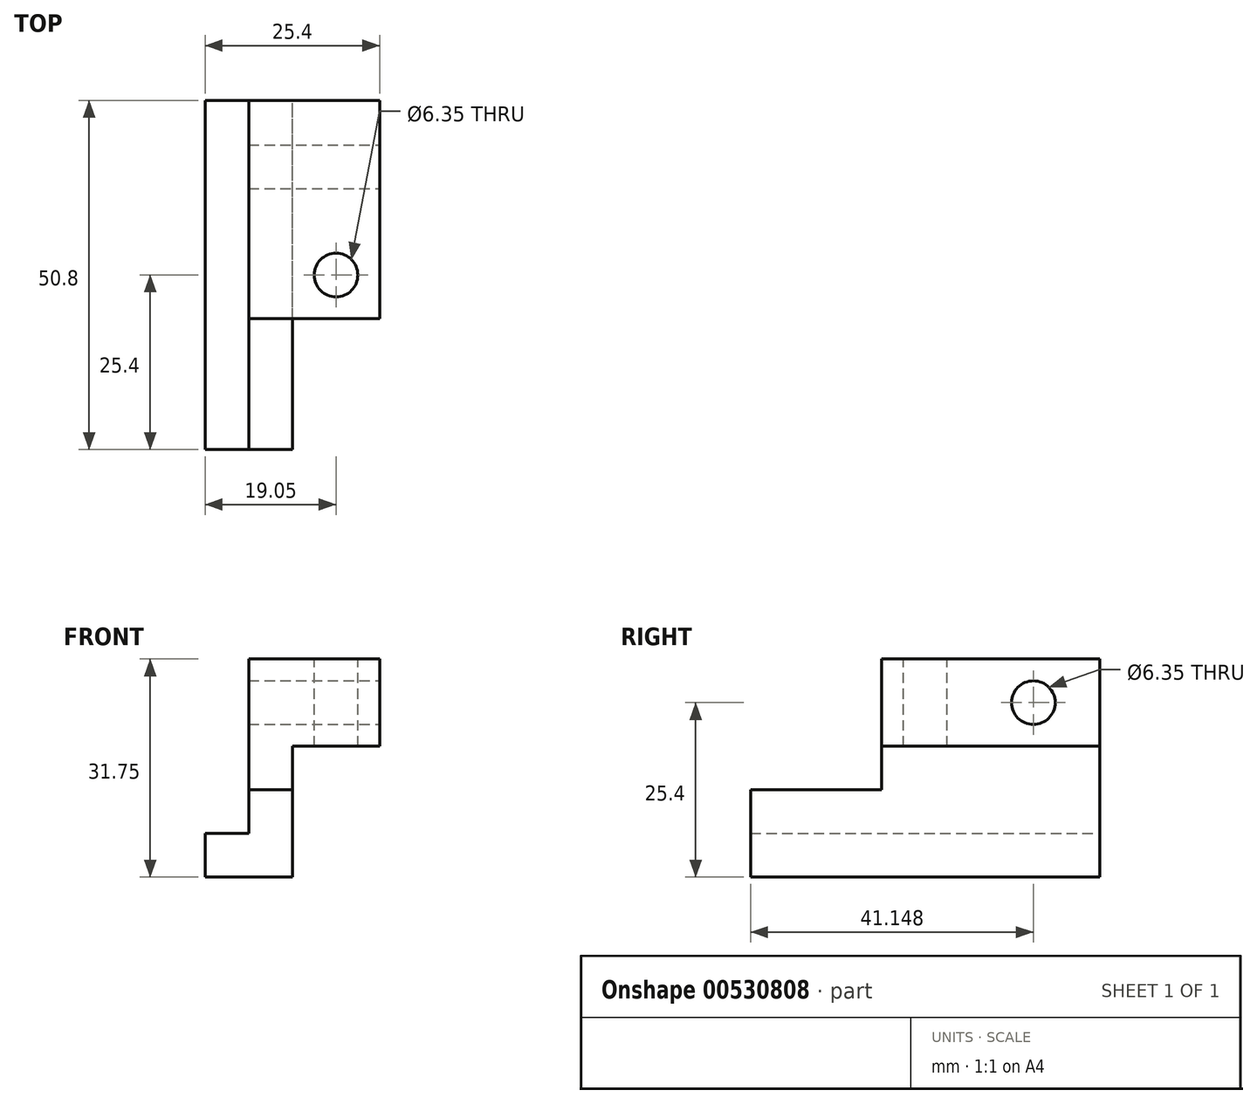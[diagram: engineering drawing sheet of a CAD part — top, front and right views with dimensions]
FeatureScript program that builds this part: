
annotation { "Feature Type Name" : "Feature", "Feature Type Description" : "" }
export const myFeature = defineFeature(function(context is Context, id is Id, definition is map)
    precondition{}
    {
        {
            var Q0;
            Q0=qCreatedBy(makeId("Front.planeOp"),FACE);
            var sketch = newSketch(context, id + "F0", { "sketchPlane" : qUnion([Q0])});
            skLineSegment(sketch, "E0", {"start": v(0, 0) * mm, "end": v(0, -12.7) * mm});
            skLineSegment(sketch, "E1", {"start": v(0, -12.7) * mm, "end": v(-12.7, -12.7) * mm});
            skLineSegment(sketch, "E2", {"start": v(-12.7, -12.7) * mm, "end": v(-12.7, -6.35) * mm});
            skLineSegment(sketch, "E3", {"start": v(-12.7, -6.35) * mm, "end": v(-6.35, -6.35) * mm});
            skLineSegment(sketch, "E4", {"start": v(-6.35, -6.35) * mm, "end": v(-6.35, 0) * mm});
            skLineSegment(sketch, "E5", {"start": v(-6.35, 0) * mm, "end": v(0, 0) * mm});
            skSolve(sketch);
        }
        {
            var Q0;
            Q0=makeQuery(id+"F0.imprint","IMPRINT",FACE,{"disambiguationData":[TD([[makeQuery(id+"F0.imprint","IMPRINT",EDGE,{"derivedFrom":sQuery(id+"F0.wireOp",EDGE,"E0")}),-1.0]])]});
            extrude(context, id + "F1", {"entities" : qUnion([Q0]), "depth" : 50.8 * mm, "offsetDistance" : 25.4 * mm});
        }
        {
            var Q0;
            Q0=qCreatedBy(makeId("Front.planeOp"),FACE);
            var sketch = newSketch(context, id + "F2", { "sketchPlane" : qUnion([Q0])});
            skLineSegment(sketch, "E6", {"start": v(-6.35, 0) * mm, "end": v(-6.35, 19.05) * mm});
            skLineSegment(sketch, "E7", {"start": v(-6.35, 19.05) * mm, "end": v(12.7, 19.05) * mm});
            skLineSegment(sketch, "E8", {"start": v(12.7, 19.05) * mm, "end": v(12.7, 6.35) * mm});
            skLineSegment(sketch, "E9", {"start": v(12.7, 6.35) * mm, "end": v(0, 6.35) * mm});
            skLineSegment(sketch, "E10", {"start": v(0, 6.35) * mm, "end": v(0, 0) * mm});
            skLineSegment(sketch, "E11", {"start": v(-6.35, 0) * mm, "end": v(0, 0) * mm});
            skSolve(sketch);
        }
        {
            var Q0;
            Q0 = qSketchRegion(id + "F2", true);
            extrude(context, id + "F3", {"entities" : qUnion([Q0]), "operationType" : NewBodyOperationType.ADD, "depth" : 31.75 * mm, "offsetDistance" : 25.4 * mm});
        }
        {
            var Q0;
            Q0=qCreatedBy(makeId("Right.planeOp"),FACE);
            var sketch = newSketch(context, id + "F4", { "sketchPlane" : qUnion([Q0])});
            skCircle(sketch, "E12", {"center": v(-9.65, 12.7) * mm, "radius": 3.18 * mm});
            skSolve(sketch);
        }
        {
            var Q0;
            Q0 = qSketchRegion(id + "F4", true);
            extrude(context, id + "F5", {"entities" : qUnion([Q0]), "operationType" : NewBodyOperationType.REMOVE, "endBound" : BoundingType.SYMMETRIC, "oppositeDirection" : true, "depth" : 50.8 * mm, "offsetDistance" : 25.4 * mm});
        }
        {
            var Q0;
            Q0=qCreatedBy(makeId("Top.planeOp"),FACE);
            var sketch = newSketch(context, id + "F6", { "sketchPlane" : qUnion([Q0])});
            skCircle(sketch, "E13", {"center": v(6.35, -25.4) * mm, "radius": 3.17 * mm});
            skSolve(sketch);
        }
        {
            var Q0;
            Q0 = qSketchRegion(id + "F6", true);
            extrude(context, id + "F7", {"entities" : qUnion([Q0]), "operationType" : NewBodyOperationType.REMOVE, "endBound" : BoundingType.SYMMETRIC, "oppositeDirection" : true, "depth" : 50.8 * mm, "offsetDistance" : 25.4 * mm});
        }
    });
